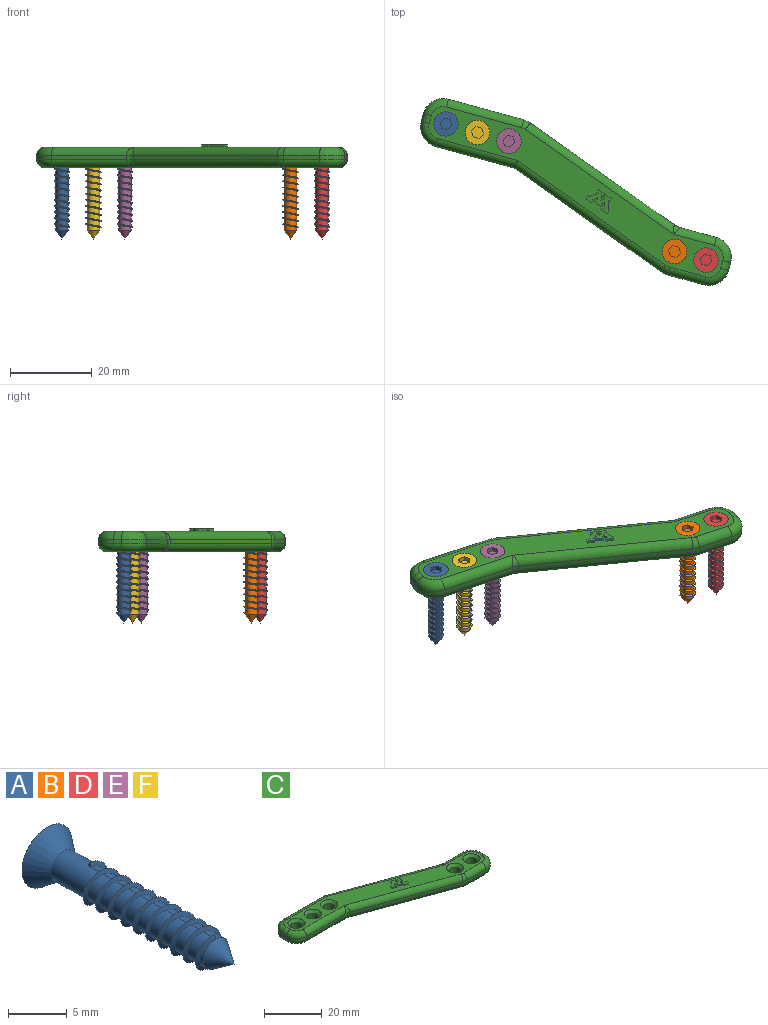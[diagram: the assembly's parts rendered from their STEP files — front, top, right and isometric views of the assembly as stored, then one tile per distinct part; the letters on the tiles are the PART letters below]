
ASSEMBLY  parts=6 mates=5
PART A: 25 faces, bbox 6x22.5x6 mm
  f0: plane 6x6mm, normal (0,1,0), area 22.4mm2, adj f12,f18,f19,f20,f21,f22,f23
  f1: cylinder r=1.5mm len=4.5mm, axis (0,1,0), area 35.3mm2, adj f2,f12,f13,f15
  f2: cylinder r=1.5mm len=3mm, axis (0,1,0), area 11.3mm2, adj f1,f3,f15,f16
  f3: cylinder r=1.5mm len=3mm, axis (0,1,0), area 11.3mm2, adj f2,f4,f15,f16
  f4: cylinder r=1.5mm len=3mm, axis (0,1,0), area 11.3mm2, adj f3,f5,f15,f16
  f5: cylinder r=1.5mm len=3mm, axis (0,1,0), area 11.3mm2, adj f4,f6,f15,f16
  f6: cylinder r=1.5mm len=3mm, axis (0,1,0), area 11.3mm2, adj f5,f7,f15,f16
  f7: cylinder r=1.5mm len=3mm, axis (0,1,0), area 11.3mm2, adj f6,f8,f15,f16
  f8: cylinder r=1.5mm len=3mm, axis (0,1,0), area 11.3mm2, adj f7,f9,f15,f16
  f9: cylinder r=1.5mm len=3mm, axis (0,1,0), area 11.3mm2, adj f8,f10,f15,f16
  f10: cylinder r=1.5mm len=3mm, axis (0,1,0), area 11.3mm2, adj f9,f11,f15,f16
  f11: cylinder r=1.5mm len=3mm, axis (0,1,0), area 7.1mm2, adj f10,f14,f16,f17
  f12: cone r=1.5mm half-angle=36.9deg, axis (0,1,0), area 35.3mm2, adj f0,f1
  f13: plane 0.4x0.3mm, normal (-1,0,0), area 0.1mm2, adj f1,f15,f16
  f14: plane 0.4x0.3mm, normal (1,0,0), area 0.1mm2, adj f11,f15,f16
  f15: bspline ~15.15x4.39mm, area 45.9mm2, adj f1,f2,f3,f4,f5,f6,f7,f8
  f16: bspline ~15.15x4.39mm, area 46mm2, adj f2,f3,f4,f5,f6,f7,f8,f9
  f17: cone r=1.5mm half-angle=34.3deg, axis (0,1,0), area 12.5mm2, adj f11
  f18: plane 1.5x1mm, normal (0,0,-1), area 1.5mm2, adj f0,f19,f23,f24
  f19: plane 1.3x1mm, normal (-0.87,0,-0.5), area 1.5mm2, adj f0,f18,f20,f24
  f20: plane 1.3x1mm, normal (-0.87,0,0.5), area 1.5mm2, adj f0,f19,f21,f24
  f21: plane 1.5x1mm, normal (0,0,1), area 1.5mm2, adj f0,f20,f22,f24
  f22: plane 1.3x1mm, normal (0.87,0,0.5), area 1.5mm2, adj f0,f21,f23,f24
  f23: plane 1.3x1mm, normal (0.87,0,-0.5), area 1.5mm2, adj f0,f18,f22,f24
  f24: plane 3x2.6mm, normal (0,1,0), area 5.8mm2, adj f18,f19,f20,f21,f22,f23
PART B: same geometry as A
PART C: 94 faces, bbox 83.1x28.2x5.6 mm
  f0: plane 78.29x23.39mm, normal (0,0,1), area 452.6mm2, adj f23,f24,f25,f26,f27,f28,f29,f30
  f1: plane 78.29x23.39mm, normal (0,0,-1), area 544.8mm2, adj f10,f11,f12,f13,f14,f15,f16,f17
  f2: plane 2x1mm, normal (-1,0,0), area 2mm2, adj f18,f26,f44,f47
  f3: plane 19.12x1mm, normal (0,-1,0), area 19.1mm2, adj f16,f24,f47,f50
  f4: plane 40.63x14.79mm, normal (-0.34,-0.94,0), area 43.2mm2, adj f15,f23,f41,f50
  f5: plane 9.12x1mm, normal (0,-1,0), area 9.1mm2, adj f17,f25,f38,f41
  f6: plane 2x1mm, normal (1,0,0), area 2mm2, adj f19,f27,f35,f38
  f7: plane 9.12x1mm, normal (0,1,0), area 9.1mm2, adj f21,f29,f35,f53
  f8: plane 40.63x14.79mm, normal (0.34,0.94,0), area 43.2mm2, adj f22,f30,f32,f53
  f9: plane 19.12x1mm, normal (0,1,0), area 19.1mm2, adj f20,f28,f32,f44
  f10: cylinder r=2mm len=4mm, axis (0,0,1), area 50.3mm2, adj f1,f55
  f11: cylinder r=2mm len=4mm, axis (0,0,1), area 50.3mm2, adj f1,f58
  f12: cylinder r=2mm len=4mm, axis (0,0,1), area 50.3mm2, adj f1,f59
  f13: cylinder r=2mm len=4mm, axis (0,0,1), area 50.3mm2, adj f1,f56
  f14: cylinder r=2mm len=4mm, axis (0,0,1), area 50.3mm2, adj f1,f57
  f15: cylinder r=2mm len=42.47mm, axis (0.94,-0.34,0), area 137.2mm2, adj f1,f4,f42,f49
  f16: cylinder r=2mm len=20.35mm, axis (1,0,0), area 61.5mm2, adj f1,f3,f48,f49
  f17: cylinder r=2mm len=9.12mm, axis (1,0,0), area 28.6mm2, adj f1,f5,f39,f42
  f18: cylinder r=2mm len=2mm, axis (0,-1,0), area 6.3mm2, adj f1,f2,f45,f48
  f19: cylinder r=2mm len=2mm, axis (0,1,0), area 6.3mm2, adj f1,f6,f36,f39
  f20: cylinder r=2mm len=19.12mm, axis (-1,0,0), area 60.1mm2, adj f1,f9,f33,f45
  f21: cylinder r=2mm len=10.35mm, axis (-1,0,0), area 30.1mm2, adj f1,f7,f36,f52
  f22: cylinder r=2mm len=42.47mm, axis (-0.94,0.34,0), area 137.2mm2, adj f1,f8,f33,f52
  f23: cylinder r=2mm len=42.47mm, axis (-0.94,0.34,0), area 137.2mm2, adj f0,f4,f40,f51
  f24: cylinder r=2mm len=20.35mm, axis (-1,0,0), area 61.5mm2, adj f0,f3,f46,f51
  f25: cylinder r=2mm len=9.12mm, axis (-1,0,0), area 28.6mm2, adj f0,f5,f37,f40
  f26: cylinder r=2mm len=2mm, axis (0,1,0), area 6.3mm2, adj f0,f2,f43,f46
  f27: cylinder r=2mm len=2mm, axis (0,-1,0), area 6.3mm2, adj f0,f6,f34,f37
  f28: cylinder r=2mm len=19.12mm, axis (1,0,0), area 60.1mm2, adj f0,f9,f31,f43
  f29: cylinder r=2mm len=10.35mm, axis (1,0,0), area 30.1mm2, adj f0,f7,f34,f54
  f30: cylinder r=2mm len=42.47mm, axis (0.94,-0.34,0), area 137.2mm2, adj f0,f8,f31,f54
  f31: torus R=3mm, axis (0,0,1), area 4.7mm2, adj f0,f28,f30,f32
  f32: cylinder r=5mm len=1.71mm, axis (0,0,-1), area 1.7mm2, adj f8,f9,f31,f33
  f33: torus R=3mm, axis (0,0,1), area 4.7mm2, adj f1,f20,f22,f32
  f34: torus R=3mm, axis (0,0,1), area 21.1mm2, adj f0,f27,f29,f35
  f35: cylinder r=5mm len=5mm, axis (0,0,1), area 7.9mm2, adj f6,f7,f34,f36
  f36: torus R=3mm, axis (0,0,1), area 21.1mm2, adj f1,f19,f21,f35
  f37: torus R=3mm, axis (0,0,1), area 21.1mm2, adj f0,f25,f27,f38
  f38: cylinder r=5mm len=5mm, axis (0,0,-1), area 7.9mm2, adj f5,f6,f37,f39
  f39: torus R=3mm, axis (0,0,1), area 21.1mm2, adj f1,f17,f19,f38
  f40: torus R=3mm, axis (0,0,1), area 4.7mm2, adj f0,f23,f25,f41
  f41: cylinder r=5mm len=1.71mm, axis (0,0,-1), area 1.7mm2, adj f4,f5,f40,f42
  f42: torus R=3mm, axis (0,0,1), area 4.7mm2, adj f1,f15,f17,f41
  f43: torus R=3mm, axis (0,0,1), area 21.1mm2, adj f0,f26,f28,f44
  f44: cylinder r=5mm len=5mm, axis (0,0,1), area 7.9mm2, adj f2,f9,f43,f45
  f45: torus R=3mm, axis (0,0,1), area 21.1mm2, adj f1,f18,f20,f44
  f46: torus R=3mm, axis (0,0,1), area 21.1mm2, adj f0,f24,f26,f47
  f47: cylinder r=5mm len=5mm, axis (0,0,-1), area 7.9mm2, adj f2,f3,f46,f48
  f48: torus R=3mm, axis (0,0,1), area 21.1mm2, adj f1,f16,f18,f47
  f49: bspline ~2.3x2.26mm, area 3.5mm2, adj f15,f16,f50
  f50: cylinder r=5mm len=1.71mm, axis (0,0,1), area 1.7mm2, adj f3,f4,f49,f51
  f51: bspline ~2.3x2.26mm, area 3.5mm2, adj f23,f24,f50
  f52: bspline ~2.3x2.26mm, area 3.5mm2, adj f21,f22,f53
  f53: cylinder r=5mm len=1.71mm, axis (0,0,1), area 1.7mm2, adj f7,f8,f52,f54
  f54: bspline ~2.3x2.26mm, area 3.5mm2, adj f29,f30,f53
  f55: cone r=2mm half-angle=45deg, axis (0,0,1), area 22.2mm2, adj f0,f10
  f56: cone r=2mm half-angle=45deg, axis (0,0,1), area 22.2mm2, adj f0,f13
  f57: cone r=2mm half-angle=45deg, axis (0,0,1), area 22.2mm2, adj f0,f14
  f58: cone r=2mm half-angle=45deg, axis (0,0,1), area 22.2mm2, adj f0,f11
  f59: cone r=2mm half-angle=45deg, axis (0,0,1), area 22.2mm2, adj f0,f12
  f60: plane 2.01x1.45mm, normal (-0.59,0.81,0), area 1.5mm2, adj f0,f61,f92,f93
  f61: plane 0.6x0.38mm, normal (0.39,0.92,0), area 0.2mm2, adj f0,f60,f62,f93
  f62: plane 0.75x0.6mm, normal (-0.94,0.33,0), area 0.5mm2, adj f0,f61,f63,f93
  f63: plane 1.79x0.65mm, normal (-0.34,-0.94,0), area 1.1mm2, adj f0,f62,f64,f93
  f64: plane 0.75x0.6mm, normal (0.94,-0.34,0), area 0.5mm2, adj f0,f63,f65,f93
  f65: plane 0.6x0.27mm, normal (0.34,0.94,0), area 0.2mm2, adj f0,f64,f66,f93
  f66: plane 1.01x0.73mm, normal (0.59,-0.81,0), area 0.8mm2, adj f0,f65,f67,f93
  f67: plane 0.6x0.51mm, normal (-0.98,-0.2,0), area 0.3mm2, adj f0,f66,f68,f93
  f68: plane 0.6x0.36mm, normal (0.34,0.94,0), area 0.2mm2, adj f0,f67,f69,f93
  f69: plane 0.79x0.6mm, normal (-0.94,0.34,0), area 0.5mm2, adj f0,f68,f70,f93
  f70: plane 1.91x0.69mm, normal (-0.34,-0.94,0), area 1.2mm2, adj f0,f69,f71,f93
  f71: plane 0.69x0.6mm, normal (0.94,-0.34,0), area 0.4mm2, adj f0,f70,f72,f93
  f72: plane 0.6x0.27mm, normal (0.34,0.94,0), area 0.2mm2, adj f0,f71,f73,f93
  f73: plane 0.65x0.6mm, normal (0.6,-0.8,0), area 0.5mm2, adj f0,f72,f74,f93
  f74: plane 1.43x0.6mm, normal (-0.98,-0.17,0), area 0.9mm2, adj f0,f73,f75,f93
  f75: plane 0.6x0.46mm, normal (0.34,0.94,0), area 0.3mm2, adj f0,f74,f76,f93
  f76: plane 0.68x0.6mm, normal (-0.94,0.34,0), area 0.4mm2, adj f0,f75,f77,f93
  f77: plane 1.79x0.65mm, normal (-0.34,-0.94,0), area 1.1mm2, adj f0,f76,f78,f93
  f78: plane 0.84x0.6mm, normal (0.94,-0.34,0), area 0.5mm2, adj f0,f77,f79,f93
  f79: plane 0.6x0.31mm, normal (0.34,0.94,0), area 0.2mm2, adj f0,f78,f80,f93
  f80: plane 2.21x0.61mm, normal (0.96,0.27,0), area 1.4mm2, adj f0,f79,f81,f93
  f81: plane 0.6x0.3mm, normal (-0.51,-0.86,0), area 0.2mm2, adj f0,f80,f82,f93
  f82: plane 0.84x0.6mm, normal (0.94,-0.34,0), area 0.5mm2, adj f0,f81,f83,f93
  f83: plane 1.67x0.61mm, normal (0.34,0.94,0), area 1.1mm2, adj f0,f82,f84,f93
  f84: plane 0.85x0.6mm, normal (-0.94,0.34,0), area 0.5mm2, adj f0,f83,f85,f93
  f85: plane 0.6x0.41mm, normal (-0.34,-0.94,0), area 0.3mm2, adj f0,f84,f86,f93
  f86: plane 0.81x0.6mm, normal (-0.59,0.81,0), area 0.6mm2, adj f0,f85,f87,f93
  f87: plane 1.05x0.6mm, normal (0.98,0.2,0), area 0.6mm2, adj f0,f86,f88,f93
  f88: plane 0.6x0.33mm, normal (-0.34,-0.94,0), area 0.2mm2, adj f0,f87,f89,f93
  f89: plane 0.74x0.6mm, normal (0.94,-0.34,0), area 0.5mm2, adj f0,f88,f90,f93
  f90: plane 1.64x0.6mm, normal (0.34,0.94,0), area 1mm2, adj f0,f89,f91,f93
  f91: plane 0.69x0.6mm, normal (-0.94,0.34,0), area 0.4mm2, adj f0,f90,f92,f93
  f92: plane 0.6x0.42mm, normal (-0.34,-0.94,0), area 0.3mm2, adj f0,f60,f91,f93
  f93: plane 6.43x5.12mm, normal (0,0,1), area 13.7mm2, adj f60,f61,f62,f63,f64,f65,f66,f67
PART D: same geometry as A
PART E: same geometry as A
PART F: same geometry as A
PLACE A rot(axis=(0.28,-0.68,-0.68),148.8deg) t=(-11.83,3.79,41.64)mm
PLACE B rot(axis=(0.28,-0.68,-0.68),148.8deg) t=(44.2,-27.47,41.64)mm
PLACE C rot(axis=(0,0,-1),15.3deg) t=(-16.04,11.16,36.64)mm
PLACE D rot(axis=(0.28,-0.68,-0.68),148.8deg) t=(51.92,-29.58,41.64)mm
PLACE E rot(axis=(0.28,-0.68,-0.68),148.8deg) t=(3.61,-0.42,41.64)mm
PLACE F rot(axis=(0.28,-0.68,-0.68),148.8deg) t=(-4.11,1.69,41.64)mm
MATE cylindrical F.f1 <-> C.f11  axis (0,0,1) through (-4.11,1.69,39.64)mm
MATE cylindrical B.f1 <-> C.f13  axis (0,0,1) through (44.2,-27.47,39.64)mm
MATE cylindrical A.f1 <-> C.f14  axis (0,0,1) through (-11.83,3.79,39.64)mm
MATE cylindrical D.f1 <-> C.f10  axis (0,0,1) through (51.92,-29.58,39.64)mm
MATE cylindrical E.f1 <-> C.f12  axis (0,0,1) through (3.61,-0.42,39.64)mm
